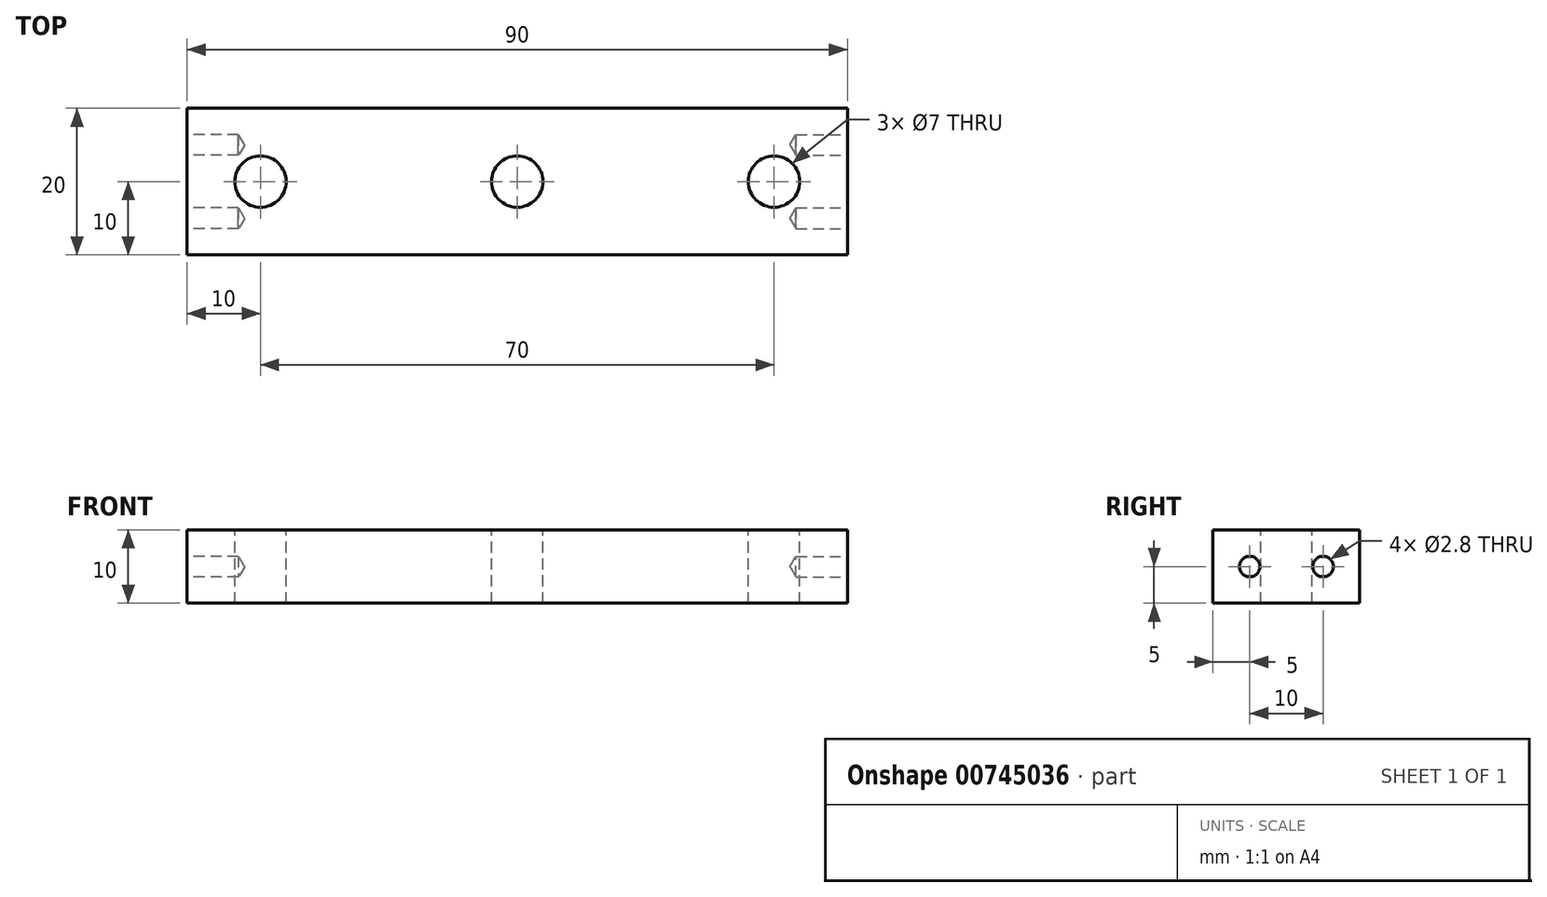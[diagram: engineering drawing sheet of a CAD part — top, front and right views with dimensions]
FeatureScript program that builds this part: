
annotation { "Feature Type Name" : "Feature", "Feature Type Description" : "" }
export const myFeature = defineFeature(function(context is Context, id is Id, definition is map)
    precondition{}
    {
        {
            var Q0;
            Q0=qCreatedBy(makeId("Top.planeOp"),FACE);
            var sketch = newSketch(context, id + "F0", { "sketchPlane" : qUnion([Q0])});
            skLineSegment(sketch, "E0.bottom", {"start": v(45, -10) * mm, "end": v(-45, -10) * mm});
            skLineSegment(sketch, "E0.top", {"start": v(45, 10) * mm, "end": v(-45, 10) * mm});
            skLineSegment(sketch, "E0.left", {"start": v(45, -10) * mm, "end": v(45, 10) * mm});
            skLineSegment(sketch, "E0.right", {"start": v(-45, -10) * mm, "end": v(-45, 10) * mm});
            skPoint(sketch, "E0.middle", {"position": v(0, 0) * mm});
            skSolve(sketch);
        }
        {
            var Q0;
            Q0=makeQuery(id+"F0.imprint","IMPRINT",FACE,{"disambiguationData":[TD([[makeQuery(id+"F0.imprint","IMPRINT",EDGE,{"derivedFrom":sQuery(id+"F0.wireOp",EDGE,"E0.bottom")}),-1.0]])]});
            extrude(context, id + "F1", {"entities" : qUnion([Q0]), "depth" : 10 * mm, "offsetDistance" : 25 * mm});
        }
        {
            var Q0;
            Q0=makeQuery(id+"F1.opExtrude","SWEPT_FACE",FACE,{"disambiguationData":[OSD([sQuery(id+"F0.wireOp",EDGE,"E0.right")])]});
            var sketch = newSketch(context, id + "F2", { "sketchPlane" : qUnion([Q0])});
            skLineSegment(sketch, "E1", {"start": v(-10, 5) * mm, "end": v(10, 5) * mm, "construction": true});
            skPoint(sketch, "E2", {"position": v(-5, 5) * mm});
            skPoint(sketch, "E3", {"position": v(5, 5) * mm});
            skSolve(sketch);
        }
        {
            var Q0;
            Q0=sQuery(id+"F2.wireOp",VERTEX,"E2");
            var Q1;
            Q1=sQuery(id+"F2.wireOp",VERTEX,"E3");
            var Q2;
            Q2=makeQuery(id+"F1.opExtrude","SWEPT_BODY",BODY,{"disambiguationData":[OSD([sQuery(id+"F0.wireOp",EDGE,"E0.bottom"),sQuery(id+"F0.wireOp",EDGE,"E0.top"),sQuery(id+"F0.wireOp",EDGE,"E0.left"),sQuery(id+"F0.wireOp",EDGE,"E0.right")])]});
            hole(context, id + "F3", {"style" : HoleStyle.SIMPLE, "endStyle" : HoleEndStyle.BLIND, "holeDiameter" : 2.8 * mm, "majorDiameter" : 5 * mm, "holeDepth" : 7 * mm, "isTappedThrough" : true, "tappedDepth" : 6 * mm, "tapClearance" : 3, "locations" : qUnion([Q0, Q1]), "scope" : qUnion([Q2])});
        }
        {
            var Q0;
            Q0=makeQuery(id+"F1.opExtrude","SWEPT_FACE",FACE,{"disambiguationData":[OSD([sQuery(id+"F0.wireOp",EDGE,"E0.left")])]});
            var sketch = newSketch(context, id + "F4", { "sketchPlane" : qUnion([Q0])});
            skPoint(sketch, "E4", {"position": v(-5, 5) * mm});
            skPoint(sketch, "E4.positionSnap0", {"position": v(-10, 5) * mm});
            skPoint(sketch, "E5", {"position": v(5, 5) * mm});
            skPoint(sketch, "E5.positionSnap0", {"position": v(10, 5) * mm});
            skSolve(sketch);
        }
        {
            var Q0;
            Q0=sQuery(id+"F4.wireOp",VERTEX,"E4");
            var Q1;
            Q1=sQuery(id+"F4.wireOp",VERTEX,"E5");
            var Q2;
            Q2=makeQuery(id+"F1.opExtrude","SWEPT_BODY",BODY,{"disambiguationData":[OSD([sQuery(id+"F0.wireOp",EDGE,"E0.bottom"),sQuery(id+"F0.wireOp",EDGE,"E0.top"),sQuery(id+"F0.wireOp",EDGE,"E0.left"),sQuery(id+"F0.wireOp",EDGE,"E0.right")])]});
            hole(context, id + "F5", {"style" : HoleStyle.SIMPLE, "endStyle" : HoleEndStyle.BLIND, "holeDiameter" : 2.8 * mm, "majorDiameter" : 5 * mm, "holeDepth" : 7 * mm, "isTappedThrough" : true, "tappedDepth" : 6 * mm, "tapClearance" : 3, "locations" : qUnion([Q0, Q1]), "scope" : qUnion([Q2])});
        }
        {
            var Q0;
            Q0=makeQuery(id+"F1.opExtrude","CAP_FACE",FACE,{"disambiguationData":[OSD([sQuery(id+"F0.wireOp",EDGE,"E0.bottom"),sQuery(id+"F0.wireOp",EDGE,"E0.top"),sQuery(id+"F0.wireOp",EDGE,"E0.left"),sQuery(id+"F0.wireOp",EDGE,"E0.right")])],"isStart":false});
            var sketch = newSketch(context, id + "F6", { "sketchPlane" : qUnion([Q0])});
            skCircle(sketch, "E6", {"center": v(-35, 0) * mm, "radius": 3.5 * mm});
            skCircle(sketch, "E7", {"center": v(0, 0) * mm, "radius": 3.5 * mm});
            skCircle(sketch, "E8", {"center": v(35, 0) * mm, "radius": 3.5 * mm});
            skSolve(sketch);
        }
        {
            var Q0;
            Q0=makeQuery(id+"F6.imprint","IMPRINT",FACE,{"disambiguationData":[TD([[makeQuery(id+"F6.imprint","IMPRINT",EDGE,{"derivedFrom":sQuery(id+"F6.wireOp",EDGE,"E8")}),1.0]])]});
            var Q1;
            Q1=makeQuery(id+"F6.imprint","IMPRINT",FACE,{"disambiguationData":[TD([[makeQuery(id+"F6.imprint","IMPRINT",EDGE,{"derivedFrom":sQuery(id+"F6.wireOp",EDGE,"E7")}),1.0]])]});
            var Q2;
            Q2=makeQuery(id+"F6.imprint","IMPRINT",FACE,{"disambiguationData":[TD([[makeQuery(id+"F6.imprint","IMPRINT",EDGE,{"derivedFrom":sQuery(id+"F6.wireOp",EDGE,"E6")}),1.0]])]});
            extrude(context, id + "F7", {"entities" : qUnion([Q0, Q1, Q2]), "operationType" : NewBodyOperationType.REMOVE, "oppositeDirection" : true, "depth" : 25 * mm, "offsetDistance" : 25 * mm});
        }
    });
